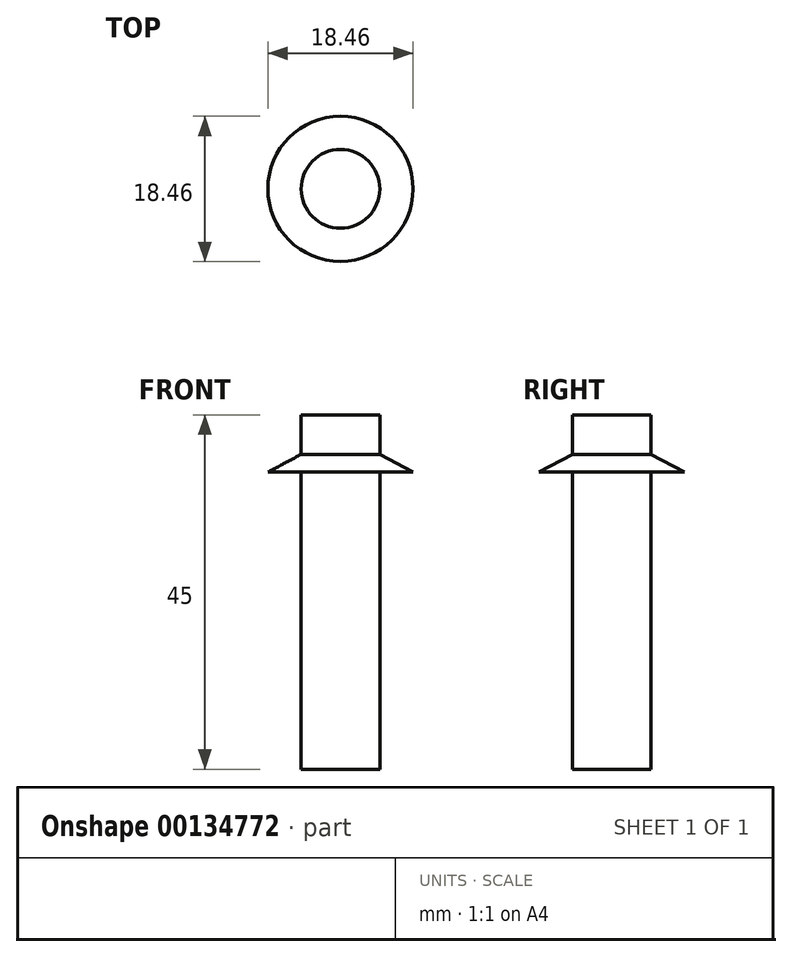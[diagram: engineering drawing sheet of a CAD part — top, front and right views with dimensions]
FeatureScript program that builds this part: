
annotation { "Feature Type Name" : "Feature", "Feature Type Description" : "" }
export const myFeature = defineFeature(function(context is Context, id is Id, definition is map)
    precondition{}
    {
        {
            var Q0;
            Q0=qCreatedBy(makeId("Front.planeOp"),FACE);
            var sketch = newSketch(context, id + "F0", { "sketchPlane" : qUnion([Q0])});
            skLineSegment(sketch, "E0", {"start": v(0, 0) * mm, "end": v(0, 24.65) * mm});
            skLineSegment(sketch, "E1", {"start": v(0, 24.65) * mm, "end": v(0, 45) * mm});
            skLineSegment(sketch, "E2", {"start": v(0, 45) * mm, "end": v(5, 45) * mm});
            skLineSegment(sketch, "E3", {"start": v(5, 45) * mm, "end": v(5, 40) * mm});
            skLineSegment(sketch, "E4", {"start": v(5, 40) * mm, "end": v(9.23, 37.75) * mm});
            skLineSegment(sketch, "E5", {"start": v(9.23, 37.75) * mm, "end": v(5, 37.75) * mm});
            skLineSegment(sketch, "E6", {"start": v(5, 37.75) * mm, "end": v(5, 0) * mm});
            skLineSegment(sketch, "E7", {"start": v(5, 0) * mm, "end": v(0, 0) * mm});
            skSolve(sketch);
        }
        {
            var Q0;
            Q0=makeQuery(id+"F0.imprint","IMPRINT",FACE,{"disambiguationData":[TD([[makeQuery(id+"F0.imprint","IMPRINT",EDGE,{"derivedFrom":sQuery(id+"F0.wireOp",EDGE,"E0")}),-1.0]])]});
            var Q1;
            Q1=sQuery(id+"F0.wireOp",EDGE,"E0");
            revolve(context, id + "F1", {"entities" : qUnion([Q0]), "axis" : qUnion([Q1]), "revolveType" : RevolveType.FULL});
        }
    });
